# Revit family: Mailboxes_4C-Salsbury_Industries-Pedestal_Mounted-Max_Height_Units
name_source: partatom
category: Specialty Equipment
revit_build: Autodesk Revit 2016 (Build: 20190507_1515(x64)
units: mm (PartAtom-declared; Revit-internal decimal feet)

## family parameters
Always vertical = Yes
Cut with Voids When Loaded = No
OmniClass Number = 23.40.90.14.11
OmniClass Title = Mail Boxes
Part Type = Normal
Room Calculation Point = No
Round Connector Dimension = Use Diameter
Shared = No
Work Plane-Based = No

## types (9) — shared parameters
4C Unit Elevation = 13.531 "
4C Unit Height = 56.719 "
Assembly Code = C1030910
Assembly Description = Mailboxes
Depth = 19 "
Height = 72 "
Manufacturer = Salsbury Industries
MasterFormat Number = 10 55 00
MasterFormat Title = Postal Specialties
OmniClass 23 Number = 23.40.90.14.11
OmniClass 23 Title = Mail Boxes
Type Comments = Pedestal Mounted 4C Horizontal Mailboxes - Front Loading
URL = www.mailboxes.com
Version = 3.0 (01/30/20)
Vertical Center Divider = Yes

## per-type parameters (varying)
| type | 4C Unit | Description | Lock Material | Model | Pedestal Height | Width |
| 3416D-8P | Mailboxes_4C-Salsbury_Industries-Front_Load-Max_Height_Units : 3716D-8P FL | Max Height Unit:  4 PL3, 1 PL4, 2 PL4.5, 1 PL5, CA | Stainless Steel - Salsbury Finish -  Polished | 3416D-8P | 12.535 " | 32.25 " |
| 3416S-3P | Mailboxes_4C-Salsbury_Industries-Front_Load-Max_Height_Units : 3716S-3P FL | Max Height Unit:  1 PL4.5, 1 PL5, 1 PL6 | Stainless Steel - Salsbury Finish -  Polished | 3416S-3P | 12.535 " | 17.496 " |
| 3416D-20 | Mailboxes_4C-Salsbury_Industries-Front_Load-Max_Height_Units : 3716D-20 FL | Max Height Unit:  20 MB1, 2 PL4.5, OM2 | Stainless Steel - Salsbury Finish -  Polished | 3416D-20 | 12.535 " | 32.25 " |
| 3416S-06 | Mailboxes_4C-Salsbury_Industries-Front_Load-Max_Height_Units : 3716S-06 FL | Max Height Unit:  6 MB1, 1 PL4.5, 1 PL3, OM2 | <By Category> | 3416S-06 | 13 " | 17.496 " |
| 3416D-15 | Mailboxes_4C-Salsbury_Industries-Front_Load-Max_Height_Units : 3716D-15 FL | Max Height Unit:  15 MB1, 2 PL4.5, 1 PL5, OM2 | Stainless Steel - Salsbury Finish -  Polished | 3416D-15 | 12.535 " | 32.25 " |
| 3416D-10 | Mailboxes_4C-Salsbury_Industries-Front_Load-Max_Height_Units : 3716D-10 FL | Max Height Unit:  10 MB1, 2 PL4.5, 2 PL5, OM2 | Stainless Steel - Salsbury Finish -  Polished | 3416D-10 | 12.535 " | 32.25 " |
| 3416D-29 | Mailboxes_4C-Salsbury_Industries-Front_Load-Max_Height_Units : 3716D-29 FL | Max Height Unit:  29 MB1, OM2 | Stainless Steel - Salsbury Finish -  Polished | 3416D-29 | 12.535 " | 32.25 " |
| 3416S-14 | Mailboxes_4C-Salsbury_Industries-Front_Load-Max_Height_Units : 3716S-14 FL | Max Height Unit:  14 MB1, OM2 | <By Category> | 3416S-14 | 13 " | 17.496 " |
| 3716S-09 | Mailboxes_4C-Salsbury_Industries-Front_Load-Max_Height_Units : 3716S-09 FL | Max Height Unit:  9 MB1, 1 PL4.5, OM2 | Stainless Steel - Salsbury Finish -  Polished | 3416S-09 | 13 " | 17.496 " |

## geometry (parser evidence)
native form markers: Extrusion x2, Sweep x21
no freeform markers — native parametric forms only
